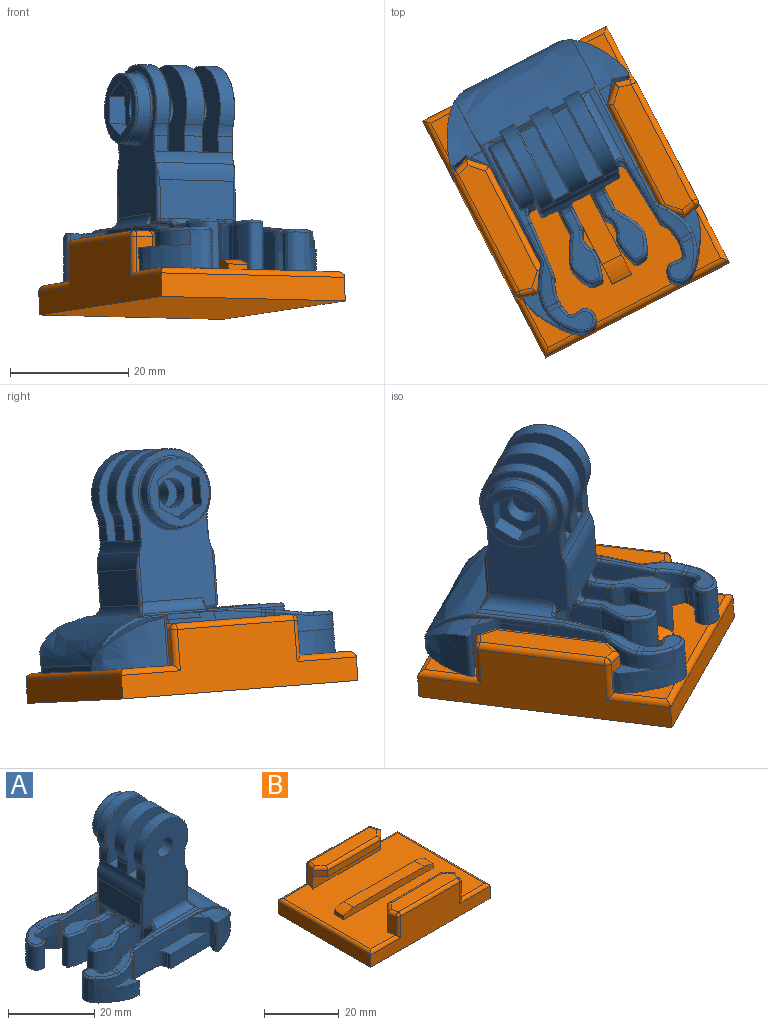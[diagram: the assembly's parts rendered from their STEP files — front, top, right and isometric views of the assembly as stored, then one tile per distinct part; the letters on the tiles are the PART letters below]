
ASSEMBLY  parts=2 mates=1
PART A: 259 faces, bbox 46.5x34.1x37.3 mm
  f0: plane 2.7x2.45mm, normal (1,0,0), area 6.6mm2, adj f24,f25,f45,f60
  f1: plane 11.4x11.4mm, normal (0,1,0), area 46.6mm2, adj f49,f50,f51,f52,f53,f54,f57
  f2: plane 27.5x14.93mm, normal (0,-1,0), area 317.2mm2, adj f17,f30,f31,f32,f33,f34,f35,f36
  f3: plane 27.5x14.93mm, normal (0,1,0), area 212.2mm2, adj f39,f40,f41,f42,f43,f44,f45,f46
  f4: plane 14.09x6.06mm, normal (1,0,0), area 84.8mm2, adj f28,f168,f253,f254,f256,f257
  f5: plane 14x6.59mm, normal (-1,0,0), area 92.2mm2, adj f18,f178,f179,f180,f181,f182,f245,f249
  f6: plane 13x3mm, normal (0,0,1), area 39mm2, adj f7,f8,f20,f27
  f7: plane 15.06x15mm, normal (0,-1,0), area 172.2mm2, adj f6,f13,f15,f20,f22,f26,f27
  f8: plane 15.06x15mm, normal (0,1,0), area 172.2mm2, adj f6,f16,f17,f20,f23,f27,f29
  f9: plane 12.75x3.25mm, normal (0,0,1), area 38.3mm2, adj f10,f11,f20,f59,f60,f64
  f10: plane 14.81x14.5mm, normal (0,-1,0), area 162.6mm2, adj f9,f14,f60,f61,f62,f63,f64
  f11: plane 15.3x15mm, normal (0,1,0), area 172.2mm2, adj f9,f13,f15,f20,f22,f24,f26,f27
  f12: cylinder r=7.5mm len=15mm, axis (0,1,0), area 72.5mm2, adj f21,f25,f43,f62
  f13: cylinder r=7.5mm len=15mm, axis (0,1,0), area 100.6mm2, adj f7,f11,f22,f26
  f14: cylinder r=2.5mm len=5mm, axis (0,1,0), area 44mm2, adj f10,f55
  f15: cylinder r=2.5mm len=5mm, axis (0,1,0), area 53.4mm2, adj f7,f11
  f16: cylinder r=7.5mm len=15mm, axis (0,1,0), area 79.9mm2, adj f8,f23,f29,f34
  f17: cylinder r=2.5mm len=5mm, axis (0,1,0), area 44mm2, adj f2,f8
  f18: cylinder r=7.5mm len=14.8mm, axis (0,-1,0), area 44mm2, adj f5,f19,f30,f39,f245,f249
  f19: cylinder r=5mm len=14.8mm, axis (0,-1,0), area 29.8mm2, adj f18,f20,f31,f40
  f20: plane 14.8x2.7mm, normal (-1,0,0), area 23.4mm2, adj f6,f7,f8,f9,f11,f19,f21,f22
  f21: cylinder r=5mm len=2.45mm, axis (0,-1,0), area 4.9mm2, adj f12,f20,f42,f63
  f22: cylinder r=5mm len=3.4mm, axis (0,-1,0), area 6.8mm2, adj f7,f11,f13,f20
  f23: cylinder r=5mm len=2.7mm, axis (0,-1,0), area 5.4mm2, adj f8,f16,f20,f33
  f24: cylinder r=5mm len=14.8mm, axis (0,-1,0), area 29.2mm2, adj f0,f11,f27,f28,f38,f47,f58,f59
  f25: cylinder r=5mm len=2.45mm, axis (0,-1,0), area 4.9mm2, adj f0,f12,f44,f61
  f26: cylinder r=5mm len=3.4mm, axis (0,-1,0), area 6.8mm2, adj f7,f11,f13,f27
  f27: plane 9.1x2.7mm, normal (1,0,0), area 16.6mm2, adj f6,f7,f8,f11,f24,f26,f29,f36
  f28: cylinder r=7.5mm len=14.8mm, axis (0,-1,0), area 44mm2, adj f4,f24,f37,f46,f253,f256
  f29: cylinder r=5mm len=2.7mm, axis (0,-1,0), area 5.4mm2, adj f8,f16,f27,f35
  f30: torus R=7.4mm, axis (0,-1,0), area 0.1mm2, adj f2,f18,f31,f245
  f31: torus R=5.1mm, axis (0,-1,0), area 0.3mm2, adj f2,f19,f30,f32
  f32: cylinder r=0.1mm len=2.7mm, axis (0,0,-1), area 0.4mm2, adj f2,f20,f31,f33
  f33: torus R=5.1mm, axis (0,-1,0), area 0.3mm2, adj f2,f23,f32,f34
  f34: torus R=7.4mm, axis (0,-1,0), area 4.6mm2, adj f2,f16,f33,f35
  f35: torus R=5.1mm, axis (0,-1,0), area 0.3mm2, adj f2,f29,f34,f36
  f36: cylinder r=0.1mm len=2.7mm, axis (0,0,1), area 0.4mm2, adj f2,f27,f35,f38
  f37: torus R=7.4mm, axis (0,-1,0), area 0.1mm2, adj f2,f28,f38,f253
  f38: torus R=5.1mm, axis (0,-1,0), area 0.3mm2, adj f2,f24,f36,f37
  f39: torus R=7.4mm, axis (0,-1,0), area 0.1mm2, adj f3,f18,f40,f249
  f40: torus R=5.1mm, axis (0,-1,0), area 0.3mm2, adj f3,f19,f39,f41
  f41: cylinder r=0.1mm len=2.7mm, axis (0,0,1), area 0.4mm2, adj f3,f20,f40,f42
  f42: torus R=5.1mm, axis (0,-1,0), area 0.3mm2, adj f3,f21,f41,f43
  f43: torus R=7.4mm, axis (0,-1,0), area 4.6mm2, adj f3,f12,f42,f44
  f44: torus R=5.1mm, axis (0,-1,0), area 0.3mm2, adj f3,f25,f43,f45
  f45: cylinder r=0.1mm len=2.7mm, axis (0,0,-1), area 0.4mm2, adj f0,f3,f44,f47
  f46: torus R=7.4mm, axis (0,-1,0), area 0.1mm2, adj f3,f28,f47,f256
  f47: torus R=5.1mm, axis (0,-1,0), area 0.3mm2, adj f3,f24,f45,f46
  f48: cylinder r=6mm len=12mm, axis (0,-1,0), area 90.5mm2, adj f56,f57
  f49: plane 4.62x3mm, normal (-1,0,0), area 13.9mm2, adj f1,f50,f54,f55
  f50: plane 4x3mm, normal (-0.5,0,0.87), area 13.9mm2, adj f1,f49,f51,f55
  f51: plane 4x3mm, normal (0.5,0,0.87), area 13.9mm2, adj f1,f50,f52,f55
  f52: plane 4.62x3mm, normal (1,0,0), area 13.9mm2, adj f1,f51,f53,f55
  f53: plane 4x3mm, normal (0.5,0,-0.87), area 13.9mm2, adj f1,f52,f54,f55
  f54: plane 4x3mm, normal (-0.5,0,-0.87), area 13.9mm2, adj f1,f49,f53,f55
  f55: plane 9.24x8mm, normal (0,1,0), area 35.8mm2, adj f14,f49,f50,f51,f52,f53,f54
  f56: torus R=6.3mm, axis (0,-1,0), area 18.1mm2, adj f3,f48
  f57: torus R=5.7mm, axis (0,1,0), area 17.4mm2, adj f1,f48
  f58: torus R=5.25mm, axis (0,-1,0), area 0mm2, adj f24,f59,f60
  f59: cylinder r=0.25mm len=3.25mm, axis (0,-1,0), area 1.2mm2, adj f9,f11,f24,f58,f60
  f60: cylinder r=0.25mm len=2.7mm, axis (0,0,1), area 1.1mm2, adj f0,f9,f10,f58,f59,f61
  f61: torus R=5.25mm, axis (0,-1,0), area 0.8mm2, adj f10,f25,f60,f62
  f62: torus R=7.25mm, axis (0,-1,0), area 11.5mm2, adj f10,f12,f61,f63
  f63: torus R=5.25mm, axis (0,-1,0), area 0.8mm2, adj f10,f21,f62,f64
  f64: cylinder r=0.25mm len=2.66mm, axis (0,0,-1), area 1mm2, adj f9,f10,f20,f63
  f65: plane 15.56x1.98mm, normal (0,0,1), area 17.4mm2, adj f68,f93,f169,f211,f212,f213,f255
  f66: plane 15.56x1.98mm, normal (0,0,1), area 17.4mm2, adj f68,f92,f167,f229,f230,f231,f258
  f67: plane 12.37x3.91mm, normal (0,0,1), area 27.2mm2, adj f181,f196,f198,f199,f200
  f68: extruded ~22.47x10.25mm, area 301.8mm2, adj f65,f66,f94,f95,f103,f118,f119,f160
  f69: plane 2.31x0.59mm, normal (-1,0,0), area 0.5mm2, adj f94,f96,f99,f101,f158,f212
  f70: plane 8.87x4.53mm, normal (0,-1,0), area 34.9mm2, adj f85,f96,f98,f122,f162,f212
  f71: plane 8.87x4.53mm, normal (0,1,0), area 34.9mm2, adj f86,f97,f115,f123,f161,f230
  f72: plane 2.31x0.59mm, normal (-1,0,0), area 0.4mm2, adj f95,f97,f106,f152,f159,f230
  f73: plane 10.98x8.41mm, normal (-0.07,-1,0), area 87.8mm2, adj f74,f107,f144,f231,f233
  f74: cylinder r=1mm len=8.8mm, axis (0,0,-1), area 12.8mm2, adj f73,f89,f144,f228,f229
  f75: cylinder r=1mm len=8.8mm, axis (0,0,-1), area 13mm2, adj f88,f89,f128,f144,f146,f184,f192
  f76: extruded ~9.82x8.41mm, area 184.1mm2, adj f77,f88,f128,f144,f146,f200
  f77: cylinder r=1mm len=8.41mm, axis (0,0,-1), area 5.3mm2, adj f76,f78,f144,f198
  f78: plane 27.15x8.52mm, normal (0,-1,0), area 112.8mm2, adj f77,f129,f144,f170,f171,f172,f188,f189
  f79: plane 27.15x8.52mm, normal (0,1,0), area 112.8mm2, adj f80,f129,f144,f175,f176,f177,f185,f186
  f80: cylinder r=1mm len=8.41mm, axis (0,0,-1), area 5.3mm2, adj f79,f81,f144,f206
  f81: extruded ~9.82x8.41mm, area 184.1mm2, adj f80,f87,f130,f144,f147,f208
  f82: cylinder r=1mm len=8.8mm, axis (0,0,-1), area 13mm2, adj f87,f90,f130,f144,f147,f183,f191
  f83: cylinder r=1mm len=8.8mm, axis (0,0,-1), area 12.8mm2, adj f84,f90,f144,f210,f211
  f84: plane 10.98x8.41mm, normal (-0.07,1,0), area 87.8mm2, adj f83,f108,f144,f213,f215
  f85: plane 8.94x8.42mm, normal (0,-1,0), area 64.5mm2, adj f70,f110,f122,f136,f144,f212,f214,f216
  f86: plane 8.94x8.42mm, normal (0,1,0), area 64.5mm2, adj f71,f111,f123,f141,f144,f230,f232,f234
  f87: plane 5.87x4.55mm, normal (0,-1,0), area 25.3mm2, adj f81,f82,f147,f191,f203,f205,f207
  f88: plane 5.87x4.55mm, normal (0,1,0), area 25.3mm2, adj f75,f76,f146,f192,f195,f197,f199
  f89: plane 9.57x3mm, normal (-1,0,0), area 23.5mm2, adj f3,f74,f75,f144,f184,f227,f252
  f90: plane 9.57x3mm, normal (-1,0,0), area 23.5mm2, adj f2,f82,f83,f144,f183,f209,f248
  f91: plane 2.91x2mm, normal (-1,0,0), area 5.8mm2, adj f171,f173,f174,f175
  f92: extruded ~13.82x3.9mm, area 15.7mm2, adj f66,f154,f231,f232,f233,f234,f235,f236
  f93: extruded ~13.82x3.9mm, area 15.7mm2, adj f65,f156,f213,f214,f215,f216,f217,f218
  f94: plane 10.32x4.97mm, normal (0,-1,0), area 5.3mm2, adj f68,f69,f103,f158,f212
  f95: plane 10.28x5mm, normal (0,1,0), area 5.7mm2, adj f68,f72,f119,f159,f160,f230
  f96: plane 9.35x0.95mm, normal (0,-1,0), area 6.6mm2, adj f69,f70,f98,f99,f162,f212
  f97: plane 9.35x0.95mm, normal (0,1,0), area 6.6mm2, adj f71,f72,f115,f152,f161,f230
  f98: cylinder r=1mm len=4.47mm, axis (0,0,-1), area 2.8mm2, adj f70,f96,f99,f101,f122,f162
  f99: extruded ~3.19x2.31mm, area 3.5mm2, adj f69,f96,f98,f101
  f100: cylinder r=0.46mm len=8.24mm, axis (0,0,-1), area 7.5mm2, adj f102,f103,f104,f144,f158
  f101: plane 4.41x3.41mm, normal (-0.61,-0.79,0), area 18.2mm2, adj f69,f98,f99,f102,f122,f158
  f102: plane 8.23x2.39mm, normal (-0.96,0.27,0), area 20.3mm2, adj f100,f101,f138,f144,f158
  f103: extruded ~10.48x8.17mm, area 77.8mm2, adj f68,f94,f100,f118,f144,f158
  f104: plane 0.2x0.14mm, normal (-1,0,0), area 0mm2, adj f100,f158
  f105: cylinder r=0.46mm len=8.23mm, axis (0,0,-1), area 7.5mm2, adj f119,f120,f144,f153,f159
  f106: plane 4.41x3.41mm, normal (-0.61,0.79,0), area 18.2mm2, adj f72,f115,f120,f123,f152,f159
  f107: cylinder r=1mm len=7.26mm, axis (0,0,-1), area 4.4mm2, adj f73,f117,f127,f144,f235,f237
  f108: cylinder r=1mm len=7.26mm, axis (0,0,-1), area 4.4mm2, adj f84,f113,f131,f144,f217,f219
  f109: plane 7.6x3.8mm, normal (0.61,-0.79,0), area 24.8mm2, adj f110,f114,f121,f135,f144,f218
  f110: cylinder r=1mm len=7.73mm, axis (0,0,-1), area 5mm2, adj f85,f109,f144,f216
  f111: cylinder r=1mm len=7.73mm, axis (0,0,-1), area 5mm2, adj f86,f112,f144,f234
  f112: plane 7.6x3.8mm, normal (0.61,0.79,0), area 24.8mm2, adj f111,f116,f142,f143,f144,f236
  f113: cylinder r=7.58mm len=6.44mm, axis (0,0,-1), area 18.3mm2, adj f108,f148,f149,f219,f221,f223
  f114: extruded ~11.3x3.41mm, area 34.2mm2, adj f109,f121,f134,f218,f220,f222,f224
  f115: cylinder r=1mm len=4.47mm, axis (0,0,-1), area 2.8mm2, adj f71,f97,f106,f123,f152,f161
  f116: extruded ~11.3x3.41mm, area 34.2mm2, adj f112,f124,f143,f236,f238,f240,f242
  f117: cylinder r=7.58mm len=6.44mm, axis (0,0,-1), area 18.3mm2, adj f107,f145,f150,f237,f239,f241
  f118: plane 18.07x1mm, normal (1,0,0), area 18mm2, adj f68,f103,f119,f144
  f119: extruded ~10.48x8.16mm, area 77.3mm2, adj f68,f95,f105,f118,f144,f159,f160
  f120: plane 8.23x2.39mm, normal (-0.96,-0.27,0), area 20.3mm2, adj f105,f106,f139,f144,f159
  f121: plane 11.31x4.93mm, normal (0,0,1), area 10.4mm2, adj f109,f114,f134,f135
  f122: plane 15.06x2.88mm, normal (0,0,1), area 33.1mm2, adj f70,f85,f98,f101,f136,f137,f138
  f123: plane 15.06x2.88mm, normal (0,0,1), area 33.1mm2, adj f71,f86,f106,f115,f139,f140,f141
  f124: extruded ~10.43x9.36mm, area 111.4mm2, adj f116,f125,f142,f143,f144,f145,f150,f244
  f125: plane 4x2.56mm, normal (0.59,-0.81,0), area 12.6mm2, adj f124,f126,f144,f145
  f126: cylinder r=1mm len=4mm, axis (0,0,-1), area 5.3mm2, adj f125,f127,f144,f145
  f127: plane 4x2.88mm, normal (-0.63,-0.77,0), area 14.9mm2, adj f107,f126,f144,f145
  f128: plane 5.63x4mm, normal (0,1,0), area 22.5mm2, adj f75,f76,f144,f146
  f129: plane 4x4mm, normal (-1,0,0), area 15.6mm2, adj f78,f79,f144,f151,f170,f177
  f130: plane 5.63x4mm, normal (0,-1,0), area 22.5mm2, adj f81,f82,f144,f147
  f131: plane 4x2.88mm, normal (-0.63,0.77,0), area 14.9mm2, adj f108,f132,f144,f148
  f132: cylinder r=1mm len=4mm, axis (0,0,-1), area 5.3mm2, adj f131,f133,f144,f148
  f133: plane 4x2.56mm, normal (0.59,0.81,0), area 12.6mm2, adj f132,f134,f144,f148
  f134: extruded ~10.43x9.36mm, area 111.4mm2, adj f114,f121,f133,f135,f144,f148,f149,f226
  f135: plane 4x2.15mm, normal (0.96,0.28,0), area 9mm2, adj f109,f121,f134,f144
  f136: cylinder r=2mm len=4mm, axis (0,0,-1), area 12.5mm2, adj f85,f122,f137,f144
  f137: plane 4x0.88mm, normal (-1,0,0), area 3.5mm2, adj f122,f136,f138,f144
  f138: plane 13.07x4mm, normal (0,-1,0), area 52.3mm2, adj f102,f122,f137,f144
  f139: plane 13.07x4mm, normal (0,1,0), area 52.3mm2, adj f120,f123,f140,f144
  f140: plane 4x0.88mm, normal (-1,0,0), area 3.5mm2, adj f123,f139,f141,f144
  f141: cylinder r=2mm len=4mm, axis (0,0,-1), area 12.5mm2, adj f86,f123,f140,f144
  f142: plane 4x2.15mm, normal (0.96,-0.28,0), area 9mm2, adj f112,f124,f143,f144
  f143: plane 11.31x4.93mm, normal (0,0,1), area 10.4mm2, adj f112,f116,f124,f142
  f144: plane 46.35x33.92mm, normal (0,0,-1), area 818.3mm2, adj f73,f74,f75,f76,f77,f78,f79,f80
  f145: plane 6.75x2.58mm, normal (0,0,-1), area 5mm2, adj f117,f124,f125,f126,f127,f150
  f146: plane 5.88x0.01mm, normal (0,0,-1), area 0mm2, adj f75,f76,f88,f128
  f147: plane 5.88x0.01mm, normal (0,0,-1), area 0mm2, adj f81,f82,f87,f130
  f148: plane 6.75x2.58mm, normal (0,0,-1), area 5mm2, adj f113,f131,f132,f133,f134,f149
  f149: cylinder r=0.5mm len=2.5mm, axis (0,0,-1), area 1.1mm2, adj f113,f134,f148,f225
  f150: cylinder r=0.5mm len=2.5mm, axis (0,0,-1), area 1.1mm2, adj f117,f124,f145,f243
  f151: plane 19.39x2mm, normal (0,0,-1), area 38.8mm2, adj f129,f170,f174,f177
  f152: extruded ~3.19x2.31mm, area 3.5mm2, adj f72,f97,f106,f115
  f153: plane 0.19x0.14mm, normal (-1,0,0), area 0mm2, adj f105,f159
  f154: cylinder r=5mm len=1.93mm, axis (0,1,0), area 1.5mm2, adj f92,f155,f239,f240
  f155: plane 6.09x5.45mm, normal (0,0,1), area 14.8mm2, adj f154,f241,f242,f243,f244
  f156: cylinder r=5mm len=1.93mm, axis (0,1,0), area 1.5mm2, adj f93,f157,f221,f222
  f157: plane 6.09x5.45mm, normal (0,0,1), area 14.8mm2, adj f156,f223,f224,f225,f226
  f158: extruded ~10.03x5.82mm, area 39.4mm2, adj f69,f94,f100,f101,f102,f103,f104
  f159: extruded ~10.03x5.82mm, area 39.4mm2, adj f72,f95,f105,f106,f119,f120,f153
  f160: plane 0.16x0.06mm, normal (-0.97,0,-0.25), area 0mm2, adj f68,f95,f119
  f161: plane 6.15x0.01mm, normal (0,0,-1), area 0mm2, adj f71,f97,f115
  f162: plane 6.15x0.01mm, normal (0,0,-1), area 0mm2, adj f70,f96,f98
  f163: plane 12.37x3.91mm, normal (0,0,1), area 27.2mm2, adj f182,f204,f206,f207,f208
  f164: plane 2x0.58mm, normal (0,0,-1), area 1.2mm2, adj f173,f179,f186,f189
  f165: plane 2.24x0.62mm, normal (0,0,-1), area 1.2mm2, adj f180,f183,f191,f247
  f166: plane 2.24x0.62mm, normal (0,0,-1), area 1.2mm2, adj f178,f184,f192,f251
  f167: cylinder r=2mm len=13.27mm, axis (1,0,0), area 37.5mm2, adj f3,f66,f227,f228,f257,f258
  f168: cylinder r=2mm len=17.49mm, axis (0,-1,0), area 27.5mm2, adj f4,f68,f255,f258
  f169: cylinder r=2mm len=13.27mm, axis (-1,0,0), area 37.5mm2, adj f2,f65,f209,f210,f254,f255
  f170: cylinder r=1mm len=19.39mm, axis (-1,0,0), area 30.5mm2, adj f78,f129,f151,f172
  f171: cylinder r=1mm len=2.91mm, axis (0,0,1), area 4.6mm2, adj f78,f91,f172,f190
  f172: bspline ~2.35x2.35mm, area 3.4mm2, adj f78,f170,f171,f174
  f173: cylinder r=1mm len=2mm, axis (0,1,0), area 3.1mm2, adj f91,f164,f187,f190
  f174: cylinder r=1mm len=2mm, axis (0,-1,0), area 3.1mm2, adj f91,f151,f172,f176
  f175: cylinder r=1mm len=2.91mm, axis (0,0,-1), area 4.6mm2, adj f79,f91,f176,f187
  f176: bspline ~2.35x2.35mm, area 3.4mm2, adj f79,f174,f175,f177
  f177: cylinder r=1mm len=19.39mm, axis (1,0,0), area 30.5mm2, adj f79,f129,f151,f176
  f178: cylinder r=1mm len=1.67mm, axis (0,-1,0), area 2.6mm2, adj f5,f166,f192,f250
  f179: cylinder r=1mm len=2mm, axis (0,-1,0), area 3.1mm2, adj f5,f164,f185,f188
  f180: cylinder r=1mm len=1.67mm, axis (0,-1,0), area 2.6mm2, adj f5,f165,f191,f246
  f181: cylinder r=1mm len=4.33mm, axis (0,1,0), area 3.1mm2, adj f5,f67,f193,f194,f195,f197
  f182: cylinder r=1mm len=4.33mm, axis (0,1,0), area 3.1mm2, adj f5,f163,f201,f202,f203,f205
  f183: cylinder r=1mm len=2.56mm, axis (0,1,0), area 3.5mm2, adj f82,f90,f165,f191,f248
  f184: cylinder r=1mm len=2.56mm, axis (0,1,0), area 3.5mm2, adj f75,f89,f166,f192,f252
  f185: torus R=2mm, axis (0,-1,0), area 1.9mm2, adj f79,f179,f186,f201
  f186: cylinder r=1mm len=1mm, axis (1,0,0), area 0.9mm2, adj f79,f164,f185,f187
  f187: sphere r=1mm, area 1.6mm2, adj f173,f175,f186
  f188: torus R=2mm, axis (0,-1,0), area 1.9mm2, adj f78,f179,f189,f193
  f189: cylinder r=1mm len=1mm, axis (-1,0,0), area 0.9mm2, adj f78,f164,f188,f190
  f190: sphere r=1mm, area 1mm2, adj f171,f173,f189
  f191: torus R=2mm, axis (0,1,0), area 2.8mm2, adj f82,f87,f165,f180,f183,f203
  f192: torus R=2mm, axis (0,1,0), area 2.8mm2, adj f75,f88,f166,f178,f184,f195
  f193: bspline ~1.5x1.39mm, area 0.6mm2, adj f181,f188,f194
  f194: torus R=1.5mm, axis (0,-1,0), area 0.4mm2, adj f78,f181,f193,f196
  f195: bspline ~1.5x1.41mm, area 0.9mm2, adj f88,f181,f192,f197
  f196: cylinder r=0.5mm len=3.18mm, axis (-1,0,0), area 2.5mm2, adj f67,f78,f194,f198
  f197: torus R=1.5mm, axis (0,-1,0), area 0.4mm2, adj f88,f181,f195,f199
  f198: torus R=0.5mm, axis (0,0,1), area 0.4mm2, adj f67,f77,f196,f200
  f199: cylinder r=0.5mm len=3.27mm, axis (1,0,0), area 2.6mm2, adj f67,f88,f197,f200
  f200: bspline ~9.75x4.84mm, area 16.8mm2, adj f67,f76,f198,f199
  f201: bspline ~1.5x1.42mm, area 0.6mm2, adj f182,f185,f202
  f202: torus R=1.5mm, axis (0,-1,0), area 0.4mm2, adj f79,f182,f201,f204
  f203: bspline ~1.5x1.41mm, area 0.9mm2, adj f87,f182,f191,f205
  f204: cylinder r=0.5mm len=3.18mm, axis (1,0,0), area 2.5mm2, adj f79,f163,f202,f206
  f205: torus R=1.5mm, axis (0,-1,0), area 0.4mm2, adj f87,f182,f203,f207
  f206: torus R=0.5mm, axis (0,0,1), area 0.4mm2, adj f80,f163,f204,f208
  f207: cylinder r=0.5mm len=3.27mm, axis (-1,0,0), area 2.6mm2, adj f87,f163,f205,f208
  f208: bspline ~9.75x4.84mm, area 16.8mm2, adj f81,f163,f206,f207
  f209: torus R=2.5mm, axis (1,0,0), area 1.2mm2, adj f2,f90,f169,f210
  f210: bspline ~1.47x1.15mm, area 1mm2, adj f83,f169,f209,f211
  f211: torus R=1.5mm, axis (0,0,1), area 0.4mm2, adj f65,f83,f210,f213
  f212: cylinder r=0.5mm len=17.68mm, axis (-1,0,0), area 11.1mm2, adj f65,f68,f69,f70,f85,f94,f96,f214
  f213: cylinder r=0.5mm len=1.54mm, axis (-1,-0.07,0), area 1.2mm2, adj f65,f84,f93,f211,f215
  f214: bspline ~9.99x1.58mm, area 5.1mm2, adj f85,f93,f212,f216
  f215: bspline ~13.7x2.16mm, area 7.5mm2, adj f84,f93,f213,f217
  f216: bspline ~1.22x0.84mm, area 0.6mm2, adj f85,f93,f110,f214,f218
  f217: bspline ~0.83x0.66mm, area 0.4mm2, adj f93,f108,f215,f219
  f218: bspline ~10.06x7.87mm, area 1.3mm2, adj f93,f109,f114,f216,f220
  f219: bspline ~6.88x2.33mm, area 3.1mm2, adj f93,f108,f113,f217,f221
  f220: bspline ~6.79x2.52mm, area 4.8mm2, adj f93,f114,f218,f222
  f221: bspline ~2.93x0.83mm, area 0.6mm2, adj f113,f156,f219,f223
  f222: bspline ~2.38x0.83mm, area 0.7mm2, adj f114,f156,f220,f224
  f223: torus R=8.08mm, axis (0,0,-1), area 1.6mm2, adj f113,f157,f221,f225
  f224: bspline ~5.99x3.34mm, area 4.3mm2, adj f114,f157,f222,f226
  f225: torus R=1mm, axis (0,0,-1), area 0.5mm2, adj f149,f157,f223,f226
  f226: bspline ~4.53x3.86mm, area 7.7mm2, adj f134,f157,f224,f225
  f227: torus R=2.5mm, axis (-1,0,0), area 1.2mm2, adj f3,f89,f167,f228
  f228: bspline ~1.47x1.15mm, area 1mm2, adj f74,f167,f227,f229
  f229: torus R=1.5mm, axis (0,0,1), area 0.4mm2, adj f66,f74,f228,f231
  f230: cylinder r=0.5mm len=17.68mm, axis (1,0,0), area 11.1mm2, adj f66,f68,f71,f72,f86,f95,f97,f232
  f231: cylinder r=0.5mm len=1.54mm, axis (-1,0.07,0), area 1.2mm2, adj f66,f73,f92,f229,f233
  f232: bspline ~9.99x1.58mm, area 5.1mm2, adj f86,f92,f230,f234
  f233: bspline ~13.7x2.16mm, area 7.5mm2, adj f73,f92,f231,f235
  f234: bspline ~1.22x0.84mm, area 0.6mm2, adj f86,f92,f111,f232,f236
  f235: bspline ~0.83x0.66mm, area 0.4mm2, adj f92,f107,f233,f237
  f236: bspline ~10.06x7.87mm, area 1.3mm2, adj f92,f112,f116,f234,f238
  f237: bspline ~6.88x2.33mm, area 3.1mm2, adj f92,f107,f117,f235,f239
  f238: bspline ~6.79x2.52mm, area 4.8mm2, adj f92,f116,f236,f240
  f239: bspline ~2.17x0.69mm, area 0.6mm2, adj f117,f154,f237,f241
  f240: bspline ~3.25x0.86mm, area 0.7mm2, adj f116,f154,f238,f242
  f241: torus R=8.08mm, axis (0,0,-1), area 1.6mm2, adj f117,f155,f239,f243
  f242: bspline ~5.99x3.34mm, area 4.3mm2, adj f116,f155,f240,f244
  f243: torus R=1mm, axis (0,0,-1), area 0.5mm2, adj f150,f155,f241,f244
  f244: bspline ~4.54x3.87mm, area 7.7mm2, adj f124,f155,f242,f243
  f245: cylinder r=0.5mm len=8.99mm, axis (0,0,1), area 6.2mm2, adj f2,f5,f18,f30,f246
  f246: torus R=0.5mm, axis (0,-1,0), area 1mm2, adj f2,f180,f245,f247
  f247: cylinder r=0.5mm len=0.59mm, axis (-1,0,0), area 0.5mm2, adj f2,f165,f246,f248
  f248: torus R=1.5mm, axis (0,-1,0), area 1mm2, adj f2,f90,f183,f247
  f249: cylinder r=0.5mm len=8.99mm, axis (0,0,-1), area 6.2mm2, adj f3,f5,f18,f39,f250
  f250: torus R=0.5mm, axis (0,-1,0), area 1mm2, adj f3,f178,f249,f251
  f251: cylinder r=0.5mm len=0.59mm, axis (1,0,0), area 0.5mm2, adj f3,f166,f250,f252
  f252: torus R=1.5mm, axis (0,-1,0), area 1mm2, adj f3,f89,f184,f251
  f253: cylinder r=0.5mm len=7.99mm, axis (0,0,-1), area 5.5mm2, adj f2,f4,f28,f37,f254
  f254: torus R=2.5mm, axis (1,0,0), area 0.3mm2, adj f4,f169,f253,f255
  f255: bspline ~2.6x2.06mm, area 1.5mm2, adj f65,f168,f169,f254
  f256: cylinder r=0.5mm len=7.99mm, axis (0,0,1), area 5.5mm2, adj f3,f4,f28,f46,f257
  f257: torus R=2.5mm, axis (1,0,0), area 0.3mm2, adj f4,f167,f256,f258
  f258: bspline ~2.6x2.06mm, area 1.5mm2, adj f66,f167,f168,f257
PART B: 55 faces, bbox 45x35x12 mm
  f0: plane 2.83x2.83mm, normal (-0.71,0.71,0), area 8mm2, adj f2,f22,f26,f33
  f1: plane 2.83x2.83mm, normal (0.71,0.71,0), area 8mm2, adj f2,f23,f26,f29
  f2: plane 19.99x2mm, normal (0,1,0), area 40mm2, adj f0,f1,f26,f30
  f3: plane 43x33mm, normal (0,0,1), area 1174.8mm2, adj f4,f5,f6,f12,f16,f20,f22,f23
  f4: plane 3.65x1.25mm, normal (-1,0,0), area 4.6mm2, adj f3,f5,f6,f15
  f5: plane 34x2.25mm, normal (0,-1,0), area 74.1mm2, adj f3,f4,f12,f13,f14,f15
  f6: plane 34x2.25mm, normal (0,1,0), area 74.1mm2, adj f3,f4,f12,f13,f14,f15
  f7: plane 35x4mm, normal (-1,0,0), area 140mm2, adj f8,f10,f11,f53
  f8: plane 45x11mm, normal (0,-1,0), area 336.4mm2, adj f7,f9,f11,f32,f36,f38,f51,f54
  f9: plane 35x4mm, normal (1,0,0), area 140mm2, adj f8,f10,f11,f50
  f10: plane 45x11mm, normal (0,1,0), area 336.4mm2, adj f7,f9,f11,f40,f45,f48,f49,f52
  f11: plane 45x35mm, normal (0,0,-1), area 1575mm2, adj f7,f8,f9,f10
  f12: plane 3.65x1.25mm, normal (1,0,0), area 4.6mm2, adj f3,f5,f6,f14
  f13: plane 26.7x3.65mm, normal (0,0,1), area 97.5mm2, adj f5,f6,f14,f15
  f14: cylinder r=7.32mm len=3.65mm, axis (0,-1,0), area 14mm2, adj f5,f6,f12,f13
  f15: cylinder r=7.32mm len=3.65mm, axis (0,-1,0), area 14mm2, adj f4,f5,f6,f13
  f16: plane 6.03x2.67mm, normal (-0.97,0.25,0), area 16.5mm2, adj f3,f17,f27,f28,f46,f48,f52
  f17: plane 2.83x2.83mm, normal (-0.71,-0.71,0), area 8mm2, adj f16,f18,f28,f44
  f18: plane 19.99x2mm, normal (0,-1,0), area 40mm2, adj f17,f19,f28,f42
  f19: plane 2.83x2.83mm, normal (0.71,-0.71,0), area 8mm2, adj f18,f20,f28,f39
  f20: plane 6.03x2.67mm, normal (0.97,0.25,0), area 16.5mm2, adj f3,f19,f27,f28,f40,f41,f49
  f21: plane 23.43x4.25mm, normal (0,0,1), area 93.9mm2, adj f39,f41,f42,f44,f45,f46
  f22: plane 6.03x2.67mm, normal (-0.97,-0.25,0), area 16.5mm2, adj f0,f3,f25,f26,f35,f38,f54
  f23: plane 6.03x2.67mm, normal (0.97,-0.25,0), area 16.5mm2, adj f1,f3,f25,f26,f31,f32,f51
  f24: plane 23.43x4.25mm, normal (0,0,1), area 93.9mm2, adj f29,f30,f31,f33,f35,f36
  f25: plane 25.64x4mm, normal (0,1,0), area 102.6mm2, adj f3,f22,f23,f26
  f26: plane 25.65x2.85mm, normal (0,0,-1), area 65.1mm2, adj f0,f1,f2,f22,f23,f25
  f27: plane 25.64x4mm, normal (0,-1,0), area 102.6mm2, adj f3,f16,f20,f28
  f28: plane 25.65x2.85mm, normal (0,0,-1), area 65.1mm2, adj f16,f17,f18,f19,f20,f27
  f29: cylinder r=1mm len=3.54mm, axis (0.71,-0.71,0), area 5.7mm2, adj f1,f24,f30,f31
  f30: cylinder r=1mm len=19.99mm, axis (1,0,0), area 30.9mm2, adj f2,f24,f29,f33
  f31: cylinder r=1mm len=2.92mm, axis (-0.25,-0.97,0), area 4mm2, adj f23,f24,f29,f34
  f32: cylinder r=1mm len=7mm, axis (0,0,1), area 8.5mm2, adj f8,f23,f34,f51
  f33: cylinder r=1mm len=3.54mm, axis (0.71,0.71,0), area 5.7mm2, adj f0,f24,f30,f35
  f34: sphere r=1mm, area 1.3mm2, adj f31,f32,f36
  f35: cylinder r=1mm len=2.92mm, axis (-0.25,0.97,0), area 4mm2, adj f22,f24,f33,f37
  f36: cylinder r=1mm len=22.34mm, axis (-1,0,0), area 35.1mm2, adj f8,f24,f34,f37
  f37: sphere r=1mm, area 1.3mm2, adj f35,f36,f38
  f38: cylinder r=1mm len=7mm, axis (0,0,-1), area 8.5mm2, adj f8,f22,f37,f54
  f39: cylinder r=1mm len=3.54mm, axis (-0.71,-0.71,0), area 5.7mm2, adj f19,f21,f41,f42
  f40: cylinder r=1mm len=7mm, axis (0,0,1), area 8.5mm2, adj f10,f20,f43,f49
  f41: cylinder r=1mm len=2.92mm, axis (0.25,-0.97,0), area 4mm2, adj f20,f21,f39,f43
  f42: cylinder r=1mm len=19.99mm, axis (-1,0,0), area 30.9mm2, adj f18,f21,f39,f44
  f43: sphere r=1mm, area 1.3mm2, adj f40,f41,f45
  f44: cylinder r=1mm len=3.54mm, axis (-0.71,0.71,0), area 5.7mm2, adj f17,f21,f42,f46
  f45: cylinder r=1mm len=22.34mm, axis (1,0,0), area 35.1mm2, adj f10,f21,f43,f47
  f46: cylinder r=1mm len=2.92mm, axis (0.25,0.97,0), area 4mm2, adj f16,f21,f44,f47
  f47: sphere r=1mm, area 1.3mm2, adj f45,f46,f48
  f48: cylinder r=1mm len=7mm, axis (0,0,-1), area 8.5mm2, adj f10,f16,f47,f52
  f49: cylinder r=1mm len=11.33mm, axis (1,0,0), area 16.2mm2, adj f3,f10,f20,f40,f50
  f50: cylinder r=1mm len=35mm, axis (0,-1,0), area 53.8mm2, adj f3,f9,f49,f51
  f51: cylinder r=1mm len=11.33mm, axis (-1,0,0), area 16.2mm2, adj f3,f8,f23,f32,f50
  f52: cylinder r=1mm len=11.33mm, axis (1,0,0), area 16.2mm2, adj f3,f10,f16,f48,f53
  f53: cylinder r=1mm len=35mm, axis (0,1,0), area 53.8mm2, adj f3,f7,f52,f54
  f54: cylinder r=1mm len=11.33mm, axis (-1,0,0), area 16.2mm2, adj f3,f8,f22,f38,f53
PLACE A rot(axis=(-0.03,0.03,1),117.5deg) t=(37.34,-2.73,6.85)mm
PLACE B rot(axis=(-0.05,-0.05,-1),62.7deg) t=(41.12,-10.22,2.42)mm
MATE slider B.f12 <-> A.f129  axis (0.46,-0.88,0.07) through (48.88,-24.91,8.59)mm
